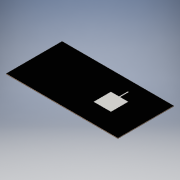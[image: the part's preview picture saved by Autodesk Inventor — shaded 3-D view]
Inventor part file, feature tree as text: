
AUTODESK INVENTOR PART (.ipt)
format: ipt  version: 2016 (Build 200138000, 138)  size: 123,392 bytes
history: native  units: in
note: dims shown in document units (in); Inventor stores cm internally (conversion verified against a paired STEP export)
features: extrude x2, sketch x2
ambient origin geometry x8: Origin, YZ Plane, XZ Plane, XY Plane, X Axis, Y Axis, Z Axis, Center Point
bodies: Solid1 (feature_tree)
feature tree (4):
  extrude  "Extrusion1"  Depth=48.0in
  extrude  "Extrusion2"  Depth=0.001in
  sketch  "Sketch1"  dims[d0=96.0in d1=48.0in]
  sketch  "Sketch2"  dims[d2=0.5in d3=0.0in d4=1.5in d5=1.5in d6=21.0in d7=7.5in d8=15.0in d9=15.0in d10=7.5in d11=90.0deg d12=0.5in d13=7.5in d14=0.001in d15=0.0in]
